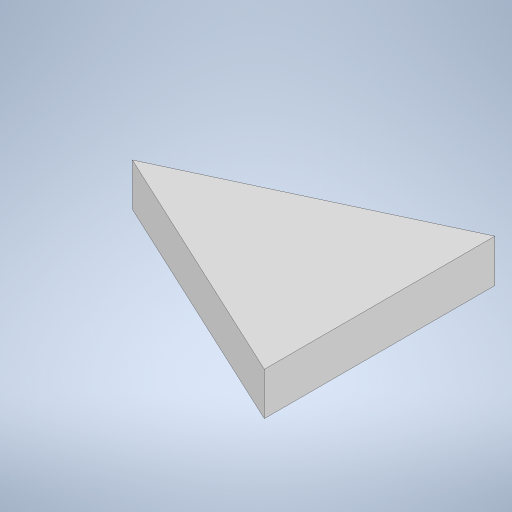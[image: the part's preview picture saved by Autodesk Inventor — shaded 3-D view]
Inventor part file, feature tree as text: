
AUTODESK INVENTOR PART (.ipt)
format: ipt  version: 2024.3 (Build 283343000, 343)  size: 224,256 bytes
history: native  units: in
note: dims shown in document units (in); Inventor stores cm internally (conversion verified against a paired STEP export)
features: extrude x2, sketch x2
ambient origin geometry x8: Origin, YZ Plane, XZ Plane, XY Plane, X Axis, Y Axis, Z Axis, Center Point
bodies: Solid1 (feature_tree)
feature tree (4):
  extrude  "Extrusion1"  Depth=4.3307in
  extrude  "Extrusion2"  Depth=0.1969in
  sketch  "Sketch1"  dims[d0=0.3436in d1=4.3307in]
  sketch  "Sketch2"  dims[d2=0.1969in d3=0.1969in d4=0.6693in d5=0.0in d6=0.0787in d7=0.0in]
